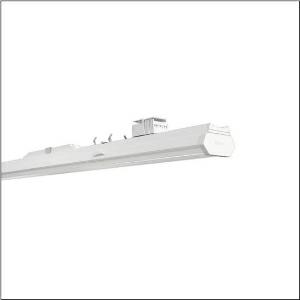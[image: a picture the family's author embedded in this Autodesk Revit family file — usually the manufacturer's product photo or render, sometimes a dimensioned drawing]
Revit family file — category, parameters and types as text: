
# Revit family: licross_r__11_protected_mo_51td1bdn49xgd_8b08
name_source: partatom
category: Lighting Fixtures
units: mm (PartAtom-declared; Revit-internal decimal feet)

## family parameters
Cut with Voids When Loaded = No
Host = Face
Light Source = No
Part Type = Normal
Room Calculation Point = No
Round Connector Dimension = Use Diameter
Shared = No

## types (1)
- --- (1 x LED, 1410 lm, 9.3 W, 4000K)
    Apparent Load = 9 VA
    CIE Flux Codes = 54 82 95 97 100
    Color Rendering = 80
    Color Temperature = 4000K
    Default Elevation = 1800 mm
    Description = Licross® 11 Protected MO, luminaire insert, of sheet steel, galvanised, coil coated, white, length: 1.500mm, width: 90mm, height: 101mm, LED rated luminous flux: 9.370lm, light colour: 840, control gear: DALI 2 (for two DALI lines), with plug, 6-pole, with phase selection, mains connection: 220..240V, AC/DC, 0/50..60Hz, rated input power: 57W, internal wiring halogen-free, for central battery installations according to DIN EN 60598-2-22, for emergency light function, without changeover relay, primary optical cover: cover, of PMMA, light emission: direct distribution, primary light characteristic: symmetric, protection rating (complete): IP54, insulation class (complete): insulation class I (protective earthing), certification: CE, ENEC, VDE, UKCA, protection symbol: D if used in an environment with non-conductive dust loads with corresponding accessories, impact resistance: IK06, permissible ambient temperature for indoor applications: -25..+35°C, standard: EN 60598-2-22, corresponds to IFS (International Featured Standards) requirements for safety and quality in the food industry, reducing of maximum allowable ambient temperature of 5°C with ceiling mounting, LABS conformity tested according to VDMA 24364:2018-05, packaging unit: 1 piece
    Height = 92 mm
    Lamp = 1 x LED
    Lamp Light Flux = 1410 lm
    Lamp Power = 9.3 W
    Lamp count = 1
    Length = 1500 mm
    Luminous efficacy = 152 lm/W
    Manufacturer = Siteco
    ModVariant = No
    Model = 51TD1BDN49XGD
    Mounting Place = Ceiling
    Mounting Type = Pendant
    Number of Poles = 1
    OnlyDefault = Yes
    Power Factor = 1
    Product Name = Licross® 11 Protected MO
    Product group = luminaire insert | ceiling pendant
    ProductGroupID = 902
    Protection Class = Protection class I
    Protection Degree = IP 54
    RLX_Detail_Level = 1
    RLX_Emergency_Light_Flux = 0 lm
    RLX_Emergency_Type = 0
    RLX_Emergency_Type_DB = No
    RlxData = <blob elided: 24801 chars, md5=3e783e47>
    Socket = socket
    Standby Power = 0 W
    System Light Flux = 1410 lm
    System Power = 9 W
    Type Comments = : DC mode (central or group accumulator) initial emergency light level
    Type Image = l_1256145.jpg
    URL = http://relux.com
    VarID = @adj_109203
    Voltage = 0 V
    Weight = 0.00 kg
    Width = 88 mm

## geometry (parser evidence)
native form markers: Blend x4, Sweep x11
no freeform markers — native parametric forms only
